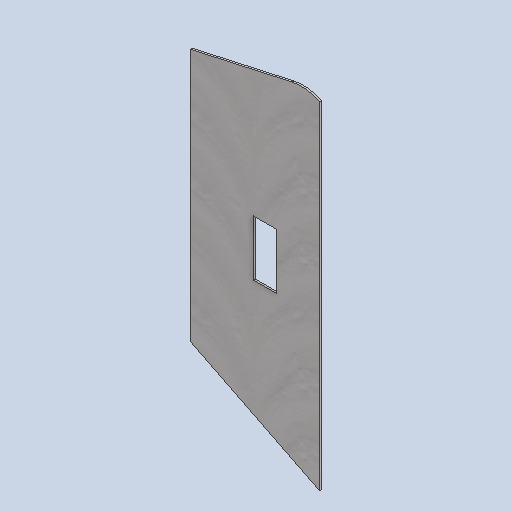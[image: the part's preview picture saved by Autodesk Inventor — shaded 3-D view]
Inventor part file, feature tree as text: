
AUTODESK INVENTOR PART (.ipt)
format: ipt  version: 2023 (Build 270158000, 158)  size: 155,648 bytes
history: native  units: mm
features: other x6, reference x5, extrude x2, sketch x2, projected_geometry x1
ambient origin geometry x8: Origin, YZ Plane, XZ Plane, XY Plane, X Axis, Y Axis, Z Axis, Center Point
bodies: Solid1 (feature_tree)
feature tree (16):
  extrude  "Extrusion1"  Depth=0.5mm TaperAngle=0.0deg
  extrude  "Extrusion2"  Depth=0.5mm
  sketch  "Sketch1"  dims[d0=0.5mm d1=0.0mm d2=0.5mm d3=0.0mm]
  reference  "Reference1"
  reference  "Reference2"
  reference  "Reference3"
  reference  "Reference4"
  reference  "Reference5"
  sketch  "Sketch2"  dims[d4=0.5mm d5=0.872665mm]
  projected_geometry  "Projected Loop1"
  other  "Assembly2"
  other  "sciana_lewa_v3:1"
  other  "pług:1"
  other  "pokrywa:1"
  other  "minisumopodsr:1"
  other  "koło_minisumo:1"
